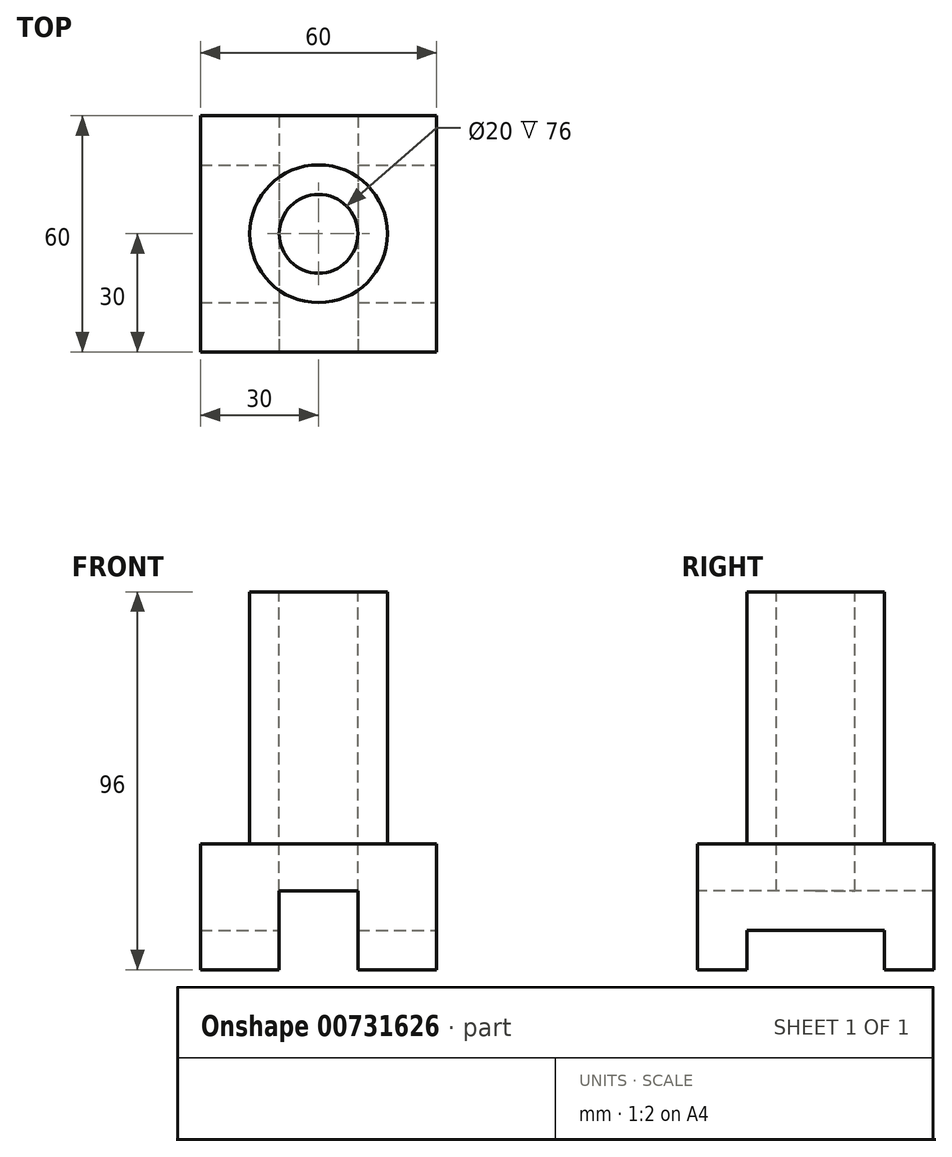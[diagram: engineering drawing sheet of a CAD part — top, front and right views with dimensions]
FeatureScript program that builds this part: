
annotation { "Feature Type Name" : "Feature", "Feature Type Description" : "" }
export const myFeature = defineFeature(function(context is Context, id is Id, definition is map)
    precondition{}
    {
        {
            var Q0;
            Q0=qCreatedBy(makeId("Top.planeOp"),FACE);
            var sketch = newSketch(context, id + "F0", { "sketchPlane" : qUnion([Q0])});
            skLineSegment(sketch, "E0.bottom", {"start": v(-30, 30) * mm, "end": v(30, 30) * mm});
            skLineSegment(sketch, "E0.top", {"start": v(-30, -30) * mm, "end": v(30, -30) * mm});
            skLineSegment(sketch, "E0.left", {"start": v(-30, 30) * mm, "end": v(-30, -30) * mm});
            skLineSegment(sketch, "E0.right", {"start": v(30, 30) * mm, "end": v(30, -30) * mm});
            skSolve(sketch);
        }
        {
            var Q0;
            Q0 = qSketchRegion(id + "F0", true);
            extrude(context, id + "F1", {"entities" : qUnion([Q0]), "depth" : 32 * mm, "offsetDistance" : 25 * mm});
        }
        {
            var Q0;
            Q0=makeQuery(id+"F1.opExtrude","CAP_FACE",FACE,{"disambiguationData":[OSD([sQuery(id+"F0.wireOp",EDGE,"E0.bottom"),sQuery(id+"F0.wireOp",EDGE,"E0.top"),sQuery(id+"F0.wireOp",EDGE,"E0.left"),sQuery(id+"F0.wireOp",EDGE,"E0.right")])],"isStart":false});
            var sketch = newSketch(context, id + "F2", { "sketchPlane" : qUnion([Q0])});
            skCircle(sketch, "E1", {"center": v(0, 0) * mm, "radius": 17.5 * mm});
            skSolve(sketch);
        }
        {
            var Q0;
            Q0=makeQuery(id+"F2.imprint","IMPRINT",FACE,{"disambiguationData":[TD([[makeQuery(id+"F2.imprint","IMPRINT",EDGE,{"derivedFrom":sQuery(id+"F2.wireOp",EDGE,"E1")}),1.0]])]});
            extrude(context, id + "F3", {"entities" : qUnion([Q0]), "operationType" : NewBodyOperationType.ADD, "depth" : 64 * mm, "offsetDistance" : 25 * mm});
        }
        {
            var Q0;
            Q0=makeQuery(id+"F1.opExtrude","SWEPT_FACE",FACE,{"disambiguationData":[OSD([sQuery(id+"F0.wireOp",EDGE,"E0.top")])]});
            var sketch = newSketch(context, id + "F4", { "sketchPlane" : qUnion([Q0])});
            skLineSegment(sketch, "E2.bottom", {"start": v(-10, 20) * mm, "end": v(10, 20) * mm});
            skLineSegment(sketch, "E2.top", {"start": v(-10, 0) * mm, "end": v(10, 0) * mm});
            skLineSegment(sketch, "E2.left", {"start": v(-10, 20) * mm, "end": v(-10, 0) * mm});
            skLineSegment(sketch, "E2.right", {"start": v(10, 20) * mm, "end": v(10, 0) * mm});
            skSolve(sketch);
        }
        {
            var Q0;
            Q0=makeQuery(id+"F4.imprint","IMPRINT",FACE,{"disambiguationData":[TD([[makeQuery(id+"F4.imprint","IMPRINT",EDGE,{"derivedFrom":sQuery(id+"F4.wireOp",EDGE,"E2.bottom")}),-1.0]])]});
            extrude(context, id + "F5", {"entities" : qUnion([Q0]), "operationType" : NewBodyOperationType.REMOVE, "oppositeDirection" : true, "depth" : 60 * mm, "offsetDistance" : 25 * mm});
        }
        {
            var Q0;
            Q0=makeQuery(id+"F1.opExtrude","SWEPT_FACE",FACE,{"disambiguationData":[OSD([sQuery(id+"F0.wireOp",EDGE,"E0.right")])]});
            var sketch = newSketch(context, id + "F6", { "sketchPlane" : qUnion([Q0])});
            skLineSegment(sketch, "E3.bottom", {"start": v(-17.5, 10) * mm, "end": v(17.5, 10) * mm});
            skLineSegment(sketch, "E3.top", {"start": v(-17.5, 0) * mm, "end": v(17.5, 0) * mm});
            skLineSegment(sketch, "E3.left", {"start": v(-17.5, 10) * mm, "end": v(-17.5, 0) * mm});
            skLineSegment(sketch, "E3.right", {"start": v(17.5, 10) * mm, "end": v(17.5, 0) * mm});
            skSolve(sketch);
        }
        {
            var Q0;
            Q0=makeQuery(id+"F6.imprint","IMPRINT",FACE,{"disambiguationData":[TD([[makeQuery(id+"F6.imprint","IMPRINT",EDGE,{"derivedFrom":sQuery(id+"F6.wireOp",EDGE,"E3.bottom")}),-1.0]])]});
            extrude(context, id + "F7", {"entities" : qUnion([Q0]), "operationType" : NewBodyOperationType.REMOVE, "oppositeDirection" : true, "depth" : 60 * mm, "offsetDistance" : 25 * mm});
        }
        {
            var Q0;
            Q0=makeQuery(id+"F3.opExtrude","CAP_FACE",FACE,{"disambiguationData":[OSD([sQuery(id+"F2.wireOp",EDGE,"E1")])],"isStart":false});
            var sketch = newSketch(context, id + "F8", { "sketchPlane" : qUnion([Q0])});
            skCircle(sketch, "E4", {"center": v(0, 0) * mm, "radius": 10 * mm});
            skSolve(sketch);
        }
        {
            var Q0;
            Q0=makeQuery(id+"F8.imprint","IMPRINT",FACE,{"disambiguationData":[TD([[makeQuery(id+"F8.imprint","IMPRINT",EDGE,{"derivedFrom":sQuery(id+"F8.wireOp",EDGE,"E4")}),1.0]])]});
            extrude(context, id + "F9", {"entities" : qUnion([Q0]), "operationType" : NewBodyOperationType.REMOVE, "oppositeDirection" : true, "depth" : 96 * mm, "offsetDistance" : 25 * mm});
        }
    });
